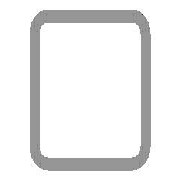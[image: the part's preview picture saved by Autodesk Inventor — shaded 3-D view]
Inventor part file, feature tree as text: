
AUTODESK INVENTOR PART (.ipt)
format: ipt  version: 2025.1 (Build 291241020, 241B)  size: 134,144 bytes
history: native  units: mm (DEFAULTED — no unit token found)
features: other x4, sketch x1, plane x1
ambient origin geometry x8: Origin, YZ Plane, XZ Plane, XY Plane, X Axis, Y Axis, Z Axis, Center Point
bodies: Solid1 (feature_tree), Body (feature_tree)
feature tree (6):
  parser-record x1  (decoder bookkeeping rows leaked as tree rows — omitted from the tree; the rows remain in map.json)
  other  "Driven Length"
  other  "Start Plane"
  other  "End Plane"
  sketch  "Sketch3"  dims[d3=1773.870082mm d4=0.0mm d7=6.0mm d9=60.0mm d11=60.0mm d12=3.0mm d13=100.0mm d14=1873.870082mm d15=30.0mm d16=30.0mm d17=90.0deg d18=1773.870082mm]
  plane  "Work Plane3"
